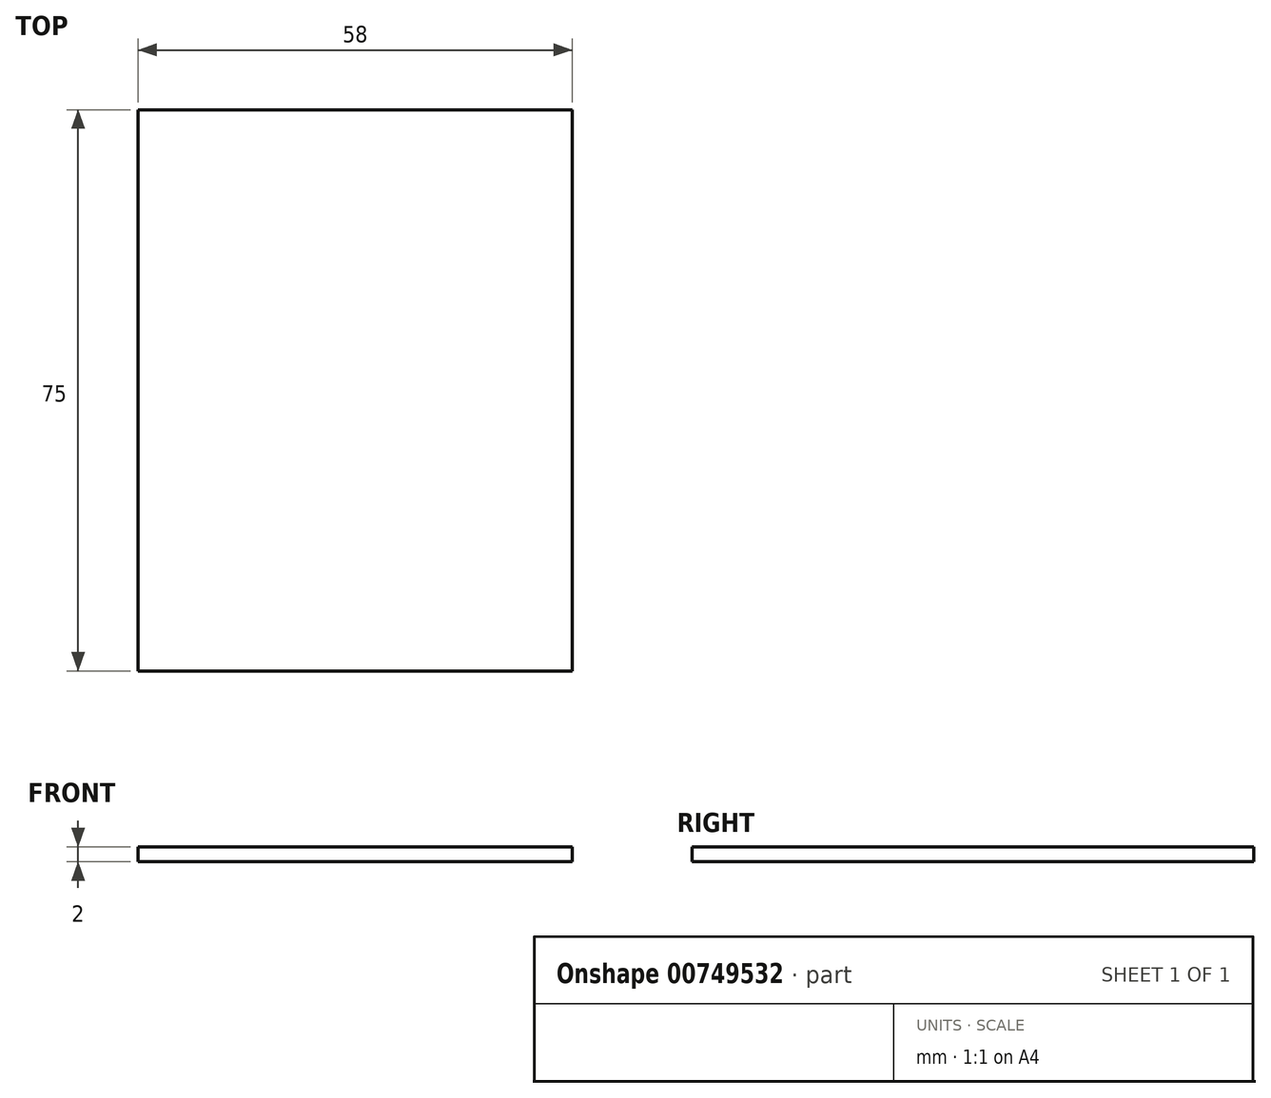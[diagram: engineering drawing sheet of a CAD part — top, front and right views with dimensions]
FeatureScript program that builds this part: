
annotation { "Feature Type Name" : "Feature", "Feature Type Description" : "" }
export const myFeature = defineFeature(function(context is Context, id is Id, definition is map)
    precondition{}
    {
        {
            var Q0;
            Q0=qCreatedBy(makeId("Top.planeOp"),FACE);
            var sketch = newSketch(context, id + "F0", { "sketchPlane" : qUnion([Q0])});
            skLineSegment(sketch, "E0", {"start": v(-29, -45) * mm, "end": v(-29, 30) * mm});
            skLineSegment(sketch, "E1", {"start": v(29, -45) * mm, "end": v(29, 30) * mm});
            skLineSegment(sketch, "E2", {"start": v(-29, 30) * mm, "end": v(29, 30) * mm});
            skLineSegment(sketch, "E3", {"start": v(-29, -45) * mm, "end": v(29, -45) * mm});
            skSolve(sketch);
        }
        {
            var Q0;
            Q0=makeQuery(id+"F0.imprint","IMPRINT",FACE,{"disambiguationData":[TD([[makeQuery(id+"F0.imprint","IMPRINT",EDGE,{"derivedFrom":sQuery(id+"F0.wireOp",EDGE,"E0")}),-1.0]])]});
            extrude(context, id + "F1", {"entities" : qUnion([Q0]), "depth" : 2 * mm, "offsetDistance" : 25 * mm});
        }
    });
